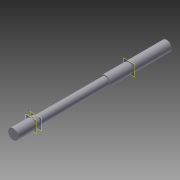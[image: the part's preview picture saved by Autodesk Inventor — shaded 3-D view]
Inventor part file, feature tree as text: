
AUTODESK INVENTOR PART (.ipt)
format: ipt  version: 2012 (Build 160160000, 160)  size: 88,576 bytes
history: native  units: in
note: dims shown in document units (in); Inventor stores cm internally (conversion verified against a paired STEP export)
features: other x3, sketch x1
ambient origin geometry x8: Origin, YZ Plane, XZ Plane, XY Plane, X Axis, Y Axis, Z Axis, Center Point
bodies: Solid1 (feature_tree)
feature tree (4):
  other  "ShaftStraight.ipt"
  other  "Solid1::ShaftStraight.ipt"
  sketch  "Sketch1"  dims[d0=0.3937in]
  other  "TaggingFeature1"
